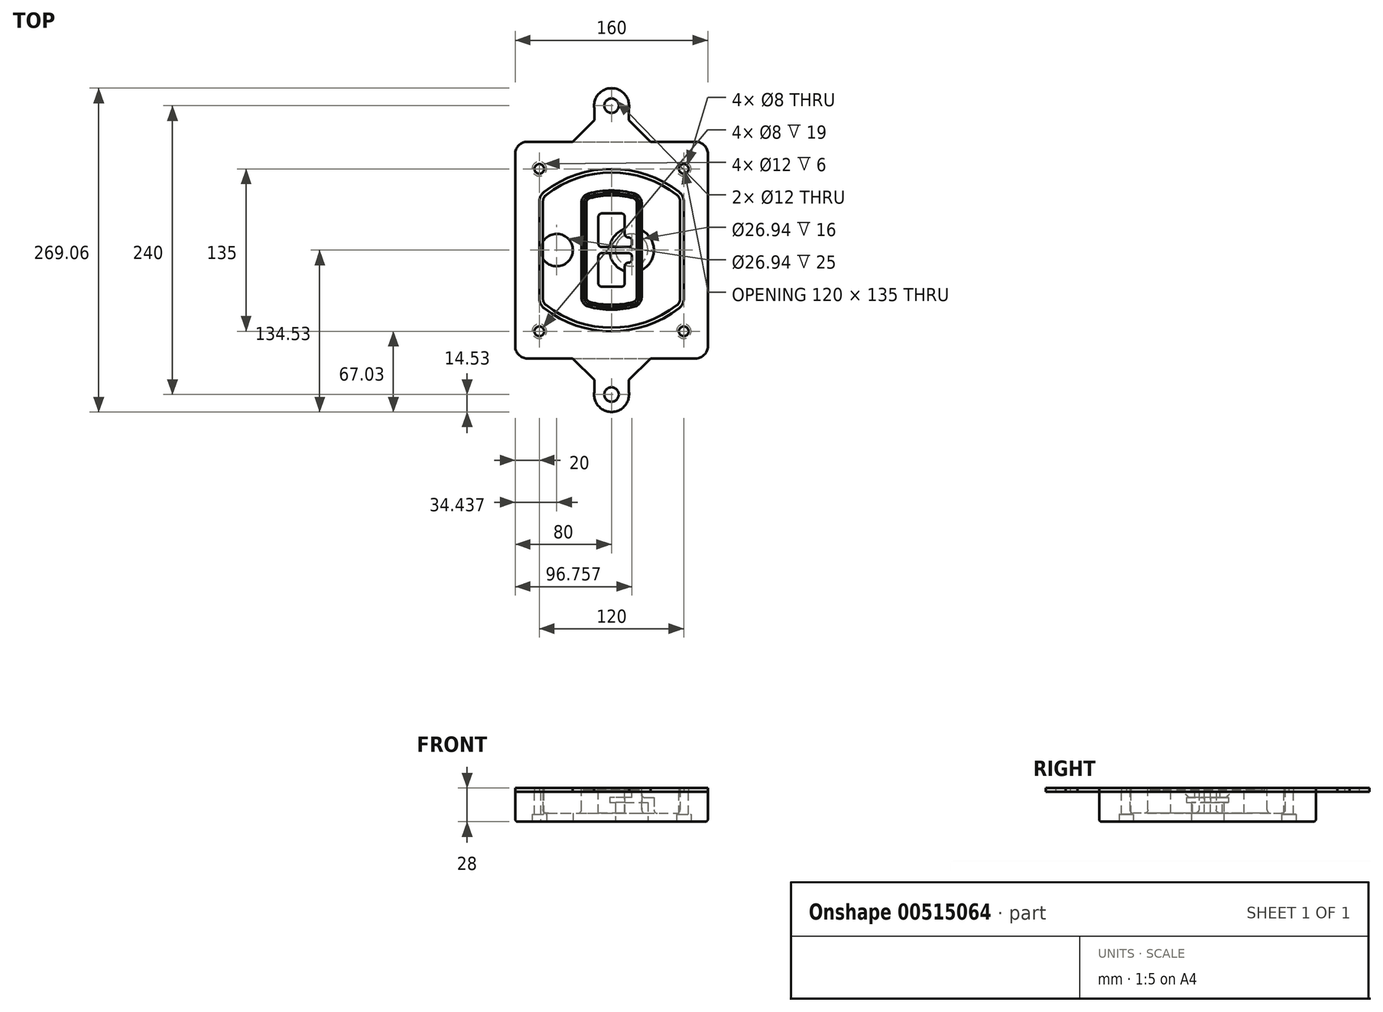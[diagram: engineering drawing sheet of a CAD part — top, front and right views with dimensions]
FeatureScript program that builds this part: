
annotation { "Feature Type Name" : "Feature", "Feature Type Description" : "" }
export const myFeature = defineFeature(function(context is Context, id is Id, definition is map)
    precondition{}
    {
        {
            var Q0;
            Q0=qCreatedBy(makeId("Top.planeOp"),FACE);
            var sketch = newSketch(context, id + "F0", { "sketchPlane" : qUnion([Q0])});
            skPoint(sketch, "E0.rect.middle", {"position": v(0, 0) * mm});
            skLineSegment(sketch, "E1.bottom", {"start": v(-70, -90) * mm, "end": v(70, -90) * mm});
            skLineSegment(sketch, "E1.top", {"start": v(-70, 90) * mm, "end": v(70, 90) * mm});
            skLineSegment(sketch, "E1.left", {"start": v(-80, -80) * mm, "end": v(-80, 80) * mm});
            skLineSegment(sketch, "E1.right", {"start": v(80, -80) * mm, "end": v(80, 80) * mm});
            skLineSegment(sketch, "E2", {"start": v(-80, 90) * mm, "end": v(80, -90) * mm, "construction": true});
            skLineSegment(sketch, "E3", {"start": v(80, 90) * mm, "end": v(-80, -90) * mm, "construction": true});
            skCircle(sketch, "E4", {"center": v(-60, 67.5) * mm, "radius": 4 * mm});
            skCircle(sketch, "E5", {"center": v(60, 67.5) * mm, "radius": 4 * mm});
            skCircle(sketch, "E6", {"center": v(60, -67.5) * mm, "radius": 4 * mm});
            skCircle(sketch, "E7", {"center": v(-60, -67.5) * mm, "radius": 4 * mm});
            skLineSegment(sketch, "E8", {"start": v(-60, 67.5) * mm, "end": v(60, 67.5) * mm, "construction": true});
            skLineSegment(sketch, "E9", {"start": v(60, 67.5) * mm, "end": v(60, -67.5) * mm, "construction": true});
            skLineSegment(sketch, "E10", {"start": v(60, -67.5) * mm, "end": v(-60, -67.5) * mm, "construction": true});
            skLineSegment(sketch, "E11", {"start": v(-60, -67.5) * mm, "end": v(-60, 67.5) * mm, "construction": true});
            skLineSegment(sketch, "E12", {"start": v(-60, 40.3) * mm, "end": v(-60, -40.3) * mm});
            skLineSegment(sketch, "E13", {"start": v(60, 40.3) * mm, "end": v(60, -40.3) * mm});
            skArc(sketch, "E14", {"start": v(56.15, 48.18) * mm, "mid": v(0, 67.5) * mm, "end": v(-56.15, 48.18) * mm});
            skArc(sketch, "E15", {"start": v(-56.15, -48.18) * mm, "mid": v(0, -67.5) * mm, "end": v(56.15, -48.18) * mm});
            skLineSegment(sketch, "E16", {"start": v(-60, 0) * mm, "end": v(60, 0) * mm, "construction": true});
            skPoint(sketch, "E17.visualSharp", {"position": v(-60, -45) * mm});
            skArc(sketch, "E17.filletArc", {"start": v(-60, -40.3) * mm, "mid": v(-58.99, -44.68) * mm, "end": v(-56.15, -48.18) * mm});
            skPoint(sketch, "E18.visualSharp", {"position": v(-60, 45) * mm});
            skArc(sketch, "E18.filletArc", {"start": v(-56.15, 48.18) * mm, "mid": v(-58.99, 44.68) * mm, "end": v(-60, 40.3) * mm});
            skPoint(sketch, "E19.visualSharp", {"position": v(60, 45) * mm});
            skArc(sketch, "E19.filletArc", {"start": v(60, 40.3) * mm, "mid": v(58.99, 44.68) * mm, "end": v(56.15, 48.18) * mm});
            skPoint(sketch, "E20.visualSharp", {"position": v(60, -45) * mm});
            skArc(sketch, "E20.filletArc", {"start": v(56.15, -48.18) * mm, "mid": v(58.99, -44.68) * mm, "end": v(60, -40.3) * mm});
            skPoint(sketch, "E21.visualSharp", {"position": v(-80, 90) * mm});
            skArc(sketch, "E21.filletArc", {"start": v(-70, 90) * mm, "mid": v(-77.07, 87.07) * mm, "end": v(-80, 80) * mm});
            skPoint(sketch, "E22.visualSharp", {"position": v(80, 90) * mm});
            skArc(sketch, "E22.filletArc", {"start": v(80, 80) * mm, "mid": v(77.07, 87.07) * mm, "end": v(70, 90) * mm});
            skPoint(sketch, "E23.visualSharp", {"position": v(80, -90) * mm});
            skArc(sketch, "E23.filletArc", {"start": v(70, -90) * mm, "mid": v(77.07, -87.07) * mm, "end": v(80, -80) * mm});
            skPoint(sketch, "E24.visualSharp", {"position": v(-80, -90) * mm});
            skArc(sketch, "E24.filletArc", {"start": v(-80, -80) * mm, "mid": v(-77.07, -87.07) * mm, "end": v(-70, -90) * mm});
            skArc(sketch, "E25.0", {"start": v(57, 40.3) * mm, "mid": v(56.3, 43.36) * mm, "end": v(54.3, 45.81) * mm});
            skLineSegment(sketch, "E25.1", {"start": v(57, 40.3) * mm, "end": v(57, -40.3) * mm});
            skArc(sketch, "E25.2", {"start": v(54.3, -45.81) * mm, "mid": v(56.3, -43.36) * mm, "end": v(57, -40.3) * mm});
            skArc(sketch, "E25.3", {"start": v(-54.3, -45.81) * mm, "mid": v(0, -64.5) * mm, "end": v(54.3, -45.81) * mm});
            skArc(sketch, "E25.4", {"start": v(-57, -40.3) * mm, "mid": v(-56.3, -43.36) * mm, "end": v(-54.3, -45.81) * mm});
            skArc(sketch, "E25.5", {"start": v(54.3, 45.81) * mm, "mid": v(0, 64.5) * mm, "end": v(-54.3, 45.81) * mm});
            skLineSegment(sketch, "E25.6", {"start": v(-57, 40.3) * mm, "end": v(-57, -40.3) * mm});
            skArc(sketch, "E25.7", {"start": v(-54.3, 45.81) * mm, "mid": v(-56.3, 43.36) * mm, "end": v(-57, 40.3) * mm});
            skArc(sketch, "E26.0", {"start": v(-58.62, 51.33) * mm, "mid": v(-62.58, 46.43) * mm, "end": v(-64, 40.3) * mm});
            skArc(sketch, "E26.1", {"start": v(58.62, 51.33) * mm, "mid": v(0, 71.5) * mm, "end": v(-58.62, 51.33) * mm});
            skArc(sketch, "E26.2", {"start": v(64, 40.3) * mm, "mid": v(62.58, 46.43) * mm, "end": v(58.62, 51.33) * mm});
            skLineSegment(sketch, "E26.3", {"start": v(64, 40.3) * mm, "end": v(64, -40.3) * mm});
            skArc(sketch, "E26.4", {"start": v(58.62, -51.33) * mm, "mid": v(62.58, -46.43) * mm, "end": v(64, -40.3) * mm});
            skLineSegment(sketch, "E26.5", {"start": v(-64, 40.3) * mm, "end": v(-64, -40.3) * mm});
            skArc(sketch, "E26.6", {"start": v(-58.62, -51.33) * mm, "mid": v(0, -71.5) * mm, "end": v(58.62, -51.33) * mm});
            skArc(sketch, "E26.7", {"start": v(-64, -40.3) * mm, "mid": v(-62.58, -46.43) * mm, "end": v(-58.62, -51.33) * mm});
            skSolve(sketch);
        }
        {
            var Q0;
            Q0=makeQuery(id+"F0.imprint","IMPRINT",FACE,{"disambiguationData":[TD([[makeQuery(id+"F0.imprint","IMPRINT",EDGE,{"derivedFrom":sQuery(id+"F0.wireOp",EDGE,"E1.bottom")}),1.0]])]});
            var Q1;
            Q1=makeQuery(id+"F0.imprint","IMPRINT",FACE,{"disambiguationData":[TD([[makeQuery(id+"F0.imprint","IMPRINT",EDGE,{"derivedFrom":sQuery(id+"F0.wireOp",EDGE,"E12")}),1.0]])]});
            var Q2;
            Q2=makeQuery(id+"F0.imprint","IMPRINT",FACE,{"disambiguationData":[TD([[makeQuery(id+"F0.imprint","IMPRINT",EDGE,{"derivedFrom":sQuery(id+"F0.wireOp",EDGE,"E25.0")}),1.0]])]});
            var Q3;
            Q3=makeQuery(id+"F0.imprint","IMPRINT",FACE,{"disambiguationData":[TD([[makeQuery(id+"F0.imprint","IMPRINT",EDGE,{"derivedFrom":sQuery(id+"F0.wireOp",EDGE,"E12")}),-1.0]])]});
            extrude(context, id + "F1", {"entities" : qUnion([Q0, Q1, Q2, Q3]), "oppositeDirection" : true, "depth" : 25 * mm});
        }
        {
            var Q0;
            Q0=makeQuery(id+"F0.imprint","IMPRINT",FACE,{"disambiguationData":[TD([[makeQuery(id+"F0.imprint","IMPRINT",EDGE,{"derivedFrom":sQuery(id+"F0.wireOp",EDGE,"E12")}),1.0]])]});
            extrude(context, id + "F2", {"entities" : qUnion([Q0]), "operationType" : NewBodyOperationType.ADD, "depth" : 3 * mm});
        }
        {
            var Q0;
            Q0=makeQuery(id+"F0.imprint","IMPRINT",FACE,{"disambiguationData":[TD([[makeQuery(id+"F0.imprint","IMPRINT",EDGE,{"derivedFrom":sQuery(id+"F0.wireOp",EDGE,"E25.0")}),1.0]])]});
            extrude(context, id + "F3", {"entities" : qUnion([Q0]), "operationType" : NewBodyOperationType.REMOVE, "oppositeDirection" : true, "depth" : 18 * mm});
        }
        {
            var Q0;
            Q0=makeQuery(id+"F2.opExtrude","CAP_FACE",FACE,{"disambiguationData":[OSD([sQuery(id+"F0.wireOp",EDGE,"E12"),sQuery(id+"F0.wireOp",EDGE,"E13"),sQuery(id+"F0.wireOp",EDGE,"E14"),sQuery(id+"F0.wireOp",EDGE,"E15"),sQuery(id+"F0.wireOp",EDGE,"E17.filletArc"),sQuery(id+"F0.wireOp",EDGE,"E18.filletArc"),sQuery(id+"F0.wireOp",EDGE,"E19.filletArc"),sQuery(id+"F0.wireOp",EDGE,"E20.filletArc"),sQuery(id+"F0.wireOp",EDGE,"E25.0"),sQuery(id+"F0.wireOp",EDGE,"E25.1"),sQuery(id+"F0.wireOp",EDGE,"E25.2"),sQuery(id+"F0.wireOp",EDGE,"E25.3"),sQuery(id+"F0.wireOp",EDGE,"E25.4"),sQuery(id+"F0.wireOp",EDGE,"E25.5"),sQuery(id+"F0.wireOp",EDGE,"E25.6"),sQuery(id+"F0.wireOp",EDGE,"E25.7")])],"isStart":false});
            var sketch = newSketch(context, id + "F4", { "sketchPlane" : qUnion([Q0])});
            skArc(sketch, "E27.0", {"start": v(-19.08, -46.97) * mm, "mid": v(0, -49.5) * mm, "end": v(19.08, -46.97) * mm});
            skArc(sketch, "E28.0", {"start": v(19.08, 46.97) * mm, "mid": v(0, 49.5) * mm, "end": v(-19.08, 46.97) * mm});
            skLineSegment(sketch, "E29", {"start": v(-25, 39.25) * mm, "end": v(-25, -39.25) * mm});
            skLineSegment(sketch, "E30", {"start": v(25, 39.25) * mm, "end": v(25, -39.25) * mm});
            skLineSegment(sketch, "E31", {"start": v(-25, 45.1) * mm, "end": v(25, 45.1) * mm, "construction": true});
            skLineSegment(sketch, "E32", {"start": v(-25, -45.1) * mm, "end": v(25, -45.1) * mm, "construction": true});
            skPoint(sketch, "E33.visualSharp", {"position": v(-25, 45.1) * mm});
            skArc(sketch, "E33.filletArc", {"start": v(-19.08, 46.97) * mm, "mid": v(-23.35, 44.11) * mm, "end": v(-25, 39.25) * mm});
            skPoint(sketch, "E34.visualSharp", {"position": v(25, 45.1) * mm});
            skArc(sketch, "E34.filletArc", {"start": v(25, 39.25) * mm, "mid": v(23.35, 44.11) * mm, "end": v(19.08, 46.97) * mm});
            skPoint(sketch, "E35.visualSharp", {"position": v(25, -45.1) * mm});
            skArc(sketch, "E35.filletArc", {"start": v(19.08, -46.97) * mm, "mid": v(23.35, -44.11) * mm, "end": v(25, -39.25) * mm});
            skPoint(sketch, "E36.visualSharp", {"position": v(-25, -45.1) * mm});
            skArc(sketch, "E36.filletArc", {"start": v(-25, -39.25) * mm, "mid": v(-23.35, -44.11) * mm, "end": v(-19.08, -46.97) * mm});
            skArc(sketch, "E37.0", {"start": v(54.3, 45.81) * mm, "mid": v(0, 64.5) * mm, "end": v(-54.3, 45.81) * mm});
            skArc(sketch, "E37.1", {"start": v(-54.3, 45.81) * mm, "mid": v(-56.3, 43.36) * mm, "end": v(-57, 40.3) * mm});
            skLineSegment(sketch, "E37.2", {"start": v(-57, 40.3) * mm, "end": v(-57, -40.3) * mm});
            skArc(sketch, "E37.3", {"start": v(-57, -40.3) * mm, "mid": v(-56.3, -43.36) * mm, "end": v(-54.3, -45.81) * mm});
            skArc(sketch, "E37.4", {"start": v(-54.3, -45.81) * mm, "mid": v(0, -64.5) * mm, "end": v(54.3, -45.81) * mm});
            skArc(sketch, "E37.5", {"start": v(54.3, -45.81) * mm, "mid": v(56.3, -43.36) * mm, "end": v(57, -40.3) * mm});
            skLineSegment(sketch, "E37.6", {"start": v(57, 40.3) * mm, "end": v(57, -40.3) * mm});
            skArc(sketch, "E37.7", {"start": v(57, 40.3) * mm, "mid": v(56.3, 43.36) * mm, "end": v(54.3, 45.81) * mm});
            skLineSegment(sketch, "E38.0", {"start": v(23, 39.25) * mm, "end": v(23, -39.25) * mm});
            skArc(sketch, "E38.1", {"start": v(18.56, -45.04) * mm, "mid": v(21.76, -42.9) * mm, "end": v(23, -39.25) * mm});
            skArc(sketch, "E38.2", {"start": v(-18.56, -45.04) * mm, "mid": v(0, -47.5) * mm, "end": v(18.56, -45.04) * mm});
            skArc(sketch, "E38.3", {"start": v(-23, -39.25) * mm, "mid": v(-21.76, -42.9) * mm, "end": v(-18.56, -45.04) * mm});
            skLineSegment(sketch, "E38.4", {"start": v(-23, 39.25) * mm, "end": v(-23, -39.25) * mm});
            skArc(sketch, "E38.5", {"start": v(23, 39.25) * mm, "mid": v(21.76, 42.9) * mm, "end": v(18.56, 45.04) * mm});
            skArc(sketch, "E38.6", {"start": v(-18.56, 45.04) * mm, "mid": v(-21.76, 42.9) * mm, "end": v(-23, 39.25) * mm});
            skArc(sketch, "E38.7", {"start": v(18.56, 45.04) * mm, "mid": v(0, 47.5) * mm, "end": v(-18.56, 45.04) * mm});
            skArc(sketch, "E39.0", {"start": v(21, 39.25) * mm, "mid": v(20.18, 41.68) * mm, "end": v(18.04, 43.1) * mm});
            skLineSegment(sketch, "E39.1", {"start": v(21, 39.25) * mm, "end": v(21, -39.25) * mm});
            skArc(sketch, "E39.2", {"start": v(18.04, -43.1) * mm, "mid": v(20.18, -41.68) * mm, "end": v(21, -39.25) * mm});
            skArc(sketch, "E39.3", {"start": v(-18.04, -43.1) * mm, "mid": v(0, -45.5) * mm, "end": v(18.04, -43.1) * mm});
            skArc(sketch, "E39.4", {"start": v(-21, -39.25) * mm, "mid": v(-20.18, -41.68) * mm, "end": v(-18.04, -43.1) * mm});
            skArc(sketch, "E39.5", {"start": v(18.04, 43.1) * mm, "mid": v(0, 45.5) * mm, "end": v(-18.04, 43.1) * mm});
            skLineSegment(sketch, "E39.6", {"start": v(-21, 39.25) * mm, "end": v(-21, -39.25) * mm});
            skArc(sketch, "E39.7", {"start": v(-18.04, 43.1) * mm, "mid": v(-20.18, 41.68) * mm, "end": v(-21, 39.25) * mm});
            skLineSegment(sketch, "E40", {"start": v(-25, 0) * mm, "end": v(25, 0) * mm, "construction": true});
            skLineSegment(sketch, "E41", {"start": v(-11, 5.5) * mm, "end": v(-11, 27.5) * mm});
            skLineSegment(sketch, "E42", {"start": v(-8, 30.5) * mm, "end": v(8, 30.5) * mm});
            skLineSegment(sketch, "E43", {"start": v(11, 27.5) * mm, "end": v(11, 13.5) * mm});
            skLineSegment(sketch, "E44", {"start": v(14, 10.5) * mm, "end": v(14, 10.5) * mm});
            skLineSegment(sketch, "E45", {"start": v(17, 7.5) * mm, "end": v(17, 5.5) * mm});
            skLineSegment(sketch, "E46", {"start": v(14, 2.5) * mm, "end": v(-8, 2.5) * mm});
            skPoint(sketch, "E47.visualSharp", {"position": v(-11, 30.5) * mm});
            skArc(sketch, "E47.filletArc", {"start": v(-8, 30.5) * mm, "mid": v(-10.12, 29.62) * mm, "end": v(-11, 27.5) * mm});
            skPoint(sketch, "E48.visualSharp", {"position": v(11, 30.5) * mm});
            skArc(sketch, "E48.filletArc", {"start": v(11, 27.5) * mm, "mid": v(10.12, 29.62) * mm, "end": v(8, 30.5) * mm});
            skPoint(sketch, "E49.visualSharp", {"position": v(11, 10.5) * mm});
            skArc(sketch, "E49.filletArc", {"start": v(11, 13.5) * mm, "mid": v(11.88, 11.38) * mm, "end": v(14, 10.5) * mm});
            skPoint(sketch, "E50.visualSharp", {"position": v(17, 10.5) * mm});
            skArc(sketch, "E50.filletArc", {"start": v(17, 7.5) * mm, "mid": v(16.12, 9.62) * mm, "end": v(14, 10.5) * mm});
            skPoint(sketch, "E51.visualSharp", {"position": v(17, 2.5) * mm});
            skArc(sketch, "E51.filletArc", {"start": v(14, 2.5) * mm, "mid": v(16.12, 3.38) * mm, "end": v(17, 5.5) * mm});
            skPoint(sketch, "E52.visualSharp", {"position": v(-11, 2.5) * mm});
            skArc(sketch, "E52.filletArc", {"start": v(-11, 5.5) * mm, "mid": v(-10.12, 3.38) * mm, "end": v(-8, 2.5) * mm});
            skLineSegment(sketch, "E53.0.MirrorCS", {"start": v(14, -2.5) * mm, "end": v(-8, -2.5) * mm});
            skArc(sketch, "E54.0.MirrorCS", {"start": v(-11, -5.5) * mm, "mid": v(-10.12, -3.38) * mm, "end": v(-8, -2.5) * mm});
            skLineSegment(sketch, "E55.0.MirrorCS", {"start": v(-11, -5.5) * mm, "end": v(-11, -27.5) * mm});
            skArc(sketch, "E56.0.MirrorCS", {"start": v(-8, -30.5) * mm, "mid": v(-10.12, -29.62) * mm, "end": v(-11, -27.5) * mm});
            skLineSegment(sketch, "E57.0.MirrorCS", {"start": v(-8, -30.5) * mm, "end": v(8, -30.5) * mm});
            skArc(sketch, "E58.0.MirrorCS", {"start": v(11, -27.5) * mm, "mid": v(10.12, -29.62) * mm, "end": v(8, -30.5) * mm});
            skLineSegment(sketch, "E59.0.MirrorCS", {"start": v(11, -27.5) * mm, "end": v(11, -13.5) * mm});
            skArc(sketch, "E60.0.MirrorCS", {"start": v(11, -13.5) * mm, "mid": v(11.88, -11.38) * mm, "end": v(14, -10.5) * mm});
            skArc(sketch, "E61.0.MirrorCS", {"start": v(17, -7.5) * mm, "mid": v(16.12, -9.62) * mm, "end": v(14, -10.5) * mm});
            skLineSegment(sketch, "E62.0.MirrorCS", {"start": v(17, -7.5) * mm, "end": v(17, -5.5) * mm});
            skArc(sketch, "E63.0.MirrorCS", {"start": v(14, -2.5) * mm, "mid": v(16.12, -3.38) * mm, "end": v(17, -5.5) * mm});
            skSolve(sketch);
        }
        {
            var Q0;
            Q0=makeQuery(id+"F4.imprint","IMPRINT",FACE,{"disambiguationData":[TD([[makeQuery(id+"F4.imprint","IMPRINT",EDGE,{"derivedFrom":sQuery(id+"F4.wireOp",EDGE,"E27.0")}),1.0]])]});
            var Q1;
            Q1=makeQuery(id+"F4.imprint","IMPRINT",FACE,{"disambiguationData":[TD([[makeQuery(id+"F4.imprint","IMPRINT",EDGE,{"derivedFrom":sQuery(id+"F4.wireOp",EDGE,"E38.0")}),-1.0]])]});
            var Q2;
            Q2=makeQuery(id+"F4.imprint","IMPRINT",FACE,{"disambiguationData":[TD([[makeQuery(id+"F4.imprint","IMPRINT",EDGE,{"derivedFrom":sQuery(id+"F4.wireOp",EDGE,"E39.0")}),1.0]])]});
            extrude(context, id + "F5", {"entities" : qUnion([Q0, Q1, Q2]), "operationType" : NewBodyOperationType.ADD, "endBound" : BoundingType.UP_TO_NEXT, "oppositeDirection" : true, "depth" : 25 * mm});
        }
        {
            var Q0;
            Q0=makeQuery(id+"F4.imprint","IMPRINT",FACE,{"disambiguationData":[TD([[makeQuery(id+"F4.imprint","IMPRINT",EDGE,{"derivedFrom":sQuery(id+"F4.wireOp",EDGE,"E38.0")}),-1.0]])]});
            extrude(context, id + "F6", {"entities" : qUnion([Q0]), "operationType" : NewBodyOperationType.REMOVE, "oppositeDirection" : true, "depth" : 2 * mm});
        }
        {
            var Q0;
            Q0=makeQuery(id+"F1.opExtrude","CAP_FACE",FACE,{"disambiguationData":[OSD([sQuery(id+"F0.wireOp",EDGE,"E1.bottom"),sQuery(id+"F0.wireOp",EDGE,"E1.top"),sQuery(id+"F0.wireOp",EDGE,"E1.left"),sQuery(id+"F0.wireOp",EDGE,"E1.right"),sQuery(id+"F0.wireOp",EDGE,"E4"),sQuery(id+"F0.wireOp",EDGE,"E5"),sQuery(id+"F0.wireOp",EDGE,"E6"),sQuery(id+"F0.wireOp",EDGE,"E7"),sQuery(id+"F0.wireOp",EDGE,"E21.filletArc"),sQuery(id+"F0.wireOp",EDGE,"E22.filletArc"),sQuery(id+"F0.wireOp",EDGE,"E23.filletArc"),sQuery(id+"F0.wireOp",EDGE,"E24.filletArc")])],"isStart":false});
            var sketch = newSketch(context, id + "F7", { "sketchPlane" : qUnion([Q0])});
            skCircle(sketch, "E64", {"center": v(16.76, 0) * mm, "radius": 13.47 * mm});
            skCircle(sketch, "E65", {"center": v(-45.56, 0) * mm, "radius": 13.47 * mm});
            skLineSegment(sketch, "E66", {"start": v(80, 0) * mm, "end": v(-80, 0) * mm});
            skCircle(sketch, "E67", {"center": v(16.76, 0) * mm, "radius": 18.47 * mm});
            skCircle(sketch, "E68", {"center": v(60, -67.5) * mm, "radius": 6 * mm});
            skCircle(sketch, "E69", {"center": v(-60, -67.5) * mm, "radius": 6 * mm});
            skCircle(sketch, "E70", {"center": v(-60, 67.5) * mm, "radius": 6 * mm});
            skCircle(sketch, "E71", {"center": v(60, 67.5) * mm, "radius": 6 * mm});
            skSolve(sketch);
        }
        {
            var Q0;
            {var subQ1=sQuery(id+"F7.wireOp",EDGE,"E66");var subQ4=sQuery(id+"F7.wireOp",EDGE,"E64");var subQ6=makeQuery(id+"F7.imprint","INTERSECT",VERTEX,{"disambiguationData":[OD(0.0)],"derivedFrom":[subQ4,subQ1]});Q0=makeQuery(id+"F7.imprint","IMPRINT",FACE,{"disambiguationData":[TD([[makeQuery(id+"F7.imprint","IMPRINT",EDGE,{"disambiguationData":[TD([[subQ6,-1.0]])],"derivedFrom":subQ4}),-1.0]])]});}
            var Q1;
            {var subQ0=sQuery(id+"F7.wireOp",EDGE,"E66");var subQ1=sQuery(id+"F7.wireOp",EDGE,"E64");var subQ3=makeQuery(id+"F7.imprint","INTERSECT",VERTEX,{"disambiguationData":[OD(0.0)],"derivedFrom":[subQ1,subQ0]});Q1=makeQuery(id+"F7.imprint","IMPRINT",FACE,{"disambiguationData":[TD([[makeQuery(id+"F7.imprint","IMPRINT",EDGE,{"disambiguationData":[TD([[subQ3,-1.0]])],"derivedFrom":subQ1}),1.0]])]});}
            var Q2;
            {var subQ0=sQuery(id+"F7.wireOp",EDGE,"E66");var subQ1=sQuery(id+"F7.wireOp",EDGE,"E64");var subQ3=makeQuery(id+"F7.imprint","INTERSECT",VERTEX,{"disambiguationData":[OD(0.0)],"derivedFrom":[subQ1,subQ0]});Q2=makeQuery(id+"F7.imprint","IMPRINT",FACE,{"disambiguationData":[TD([[makeQuery(id+"F7.imprint","IMPRINT",EDGE,{"disambiguationData":[TD([[subQ3,1.0]])],"derivedFrom":subQ1}),1.0]])]});}
            var Q3;
            {var subQ1=sQuery(id+"F7.wireOp",EDGE,"E66");var subQ4=sQuery(id+"F7.wireOp",EDGE,"E64");var subQ6=makeQuery(id+"F7.imprint","INTERSECT",VERTEX,{"disambiguationData":[OD(0.0)],"derivedFrom":[subQ4,subQ1]});Q3=makeQuery(id+"F7.imprint","IMPRINT",FACE,{"disambiguationData":[TD([[makeQuery(id+"F7.imprint","IMPRINT",EDGE,{"disambiguationData":[TD([[subQ6,1.0]])],"derivedFrom":subQ4}),-1.0]])]});}
            extrude(context, id + "F8", {"entities" : qUnion([Q0, Q1, Q2, Q3]), "operationType" : NewBodyOperationType.ADD, "oppositeDirection" : true, "depth" : 20 * mm});
        }
        {
            var Q0;
            {var subQ0=sQuery(id+"F7.wireOp",EDGE,"E66");var subQ1=sQuery(id+"F7.wireOp",EDGE,"E64");var subQ3=makeQuery(id+"F7.imprint","INTERSECT",VERTEX,{"disambiguationData":[OD(0.0)],"derivedFrom":[subQ1,subQ0]});Q0=makeQuery(id+"F7.imprint","IMPRINT",FACE,{"disambiguationData":[TD([[makeQuery(id+"F7.imprint","IMPRINT",EDGE,{"disambiguationData":[TD([[subQ3,-1.0]])],"derivedFrom":subQ1}),1.0]])]});}
            var Q1;
            {var subQ0=sQuery(id+"F7.wireOp",EDGE,"E66");var subQ1=sQuery(id+"F7.wireOp",EDGE,"E64");var subQ3=makeQuery(id+"F7.imprint","INTERSECT",VERTEX,{"disambiguationData":[OD(0.0)],"derivedFrom":[subQ1,subQ0]});Q1=makeQuery(id+"F7.imprint","IMPRINT",FACE,{"disambiguationData":[TD([[makeQuery(id+"F7.imprint","IMPRINT",EDGE,{"disambiguationData":[TD([[subQ3,1.0]])],"derivedFrom":subQ1}),1.0]])]});}
            extrude(context, id + "F9", {"entities" : qUnion([Q0, Q1]), "operationType" : NewBodyOperationType.REMOVE, "oppositeDirection" : true, "depth" : 16 * mm});
        }
        {
            var Q0;
            {var subQ0=sQuery(id+"F7.wireOp",EDGE,"E66");var subQ1=sQuery(id+"F7.wireOp",EDGE,"E65");var subQ3=makeQuery(id+"F7.imprint","INTERSECT",VERTEX,{"disambiguationData":[OD(0.0)],"derivedFrom":[subQ1,subQ0]});Q0=makeQuery(id+"F7.imprint","IMPRINT",FACE,{"disambiguationData":[TD([[makeQuery(id+"F7.imprint","IMPRINT",EDGE,{"disambiguationData":[TD([[subQ3,-1.0]])],"derivedFrom":subQ1}),1.0]])]});}
            var Q1;
            {var subQ0=sQuery(id+"F7.wireOp",EDGE,"E66");var subQ1=sQuery(id+"F7.wireOp",EDGE,"E65");var subQ3=makeQuery(id+"F7.imprint","INTERSECT",VERTEX,{"disambiguationData":[OD(0.0)],"derivedFrom":[subQ1,subQ0]});Q1=makeQuery(id+"F7.imprint","IMPRINT",FACE,{"disambiguationData":[TD([[makeQuery(id+"F7.imprint","IMPRINT",EDGE,{"disambiguationData":[TD([[subQ3,1.0]])],"derivedFrom":subQ1}),1.0]])]});}
            extrude(context, id + "F10", {"entities" : qUnion([Q0, Q1]), "operationType" : NewBodyOperationType.REMOVE, "oppositeDirection" : true, "depth" : 25 * mm});
        }
        {
            var Q0;
            Q0=makeQuery(id+"F7.imprint","IMPRINT",FACE,{"disambiguationData":[TD([[makeQuery(id+"F7.imprint","IMPRINT",EDGE,{"derivedFrom":sQuery(id+"F7.wireOp",EDGE,"E68")}),1.0]])]});
            var Q1;
            Q1=makeQuery(id+"F7.imprint","IMPRINT",FACE,{"disambiguationData":[TD([[makeQuery(id+"F7.imprint","IMPRINT",EDGE,{"derivedFrom":makeQuery(id+"F1.opExtrude","CAP_EDGE",EDGE,{"disambiguationData":[OSD([sQuery(id+"F0.wireOp",EDGE,"E5")])],"isStart":false})}),-1.0]])]});
            var Q2;
            Q2=makeQuery(id+"F7.imprint","IMPRINT",FACE,{"disambiguationData":[TD([[makeQuery(id+"F7.imprint","IMPRINT",EDGE,{"derivedFrom":sQuery(id+"F7.wireOp",EDGE,"E69")}),1.0]])]});
            var Q3;
            Q3=makeQuery(id+"F7.imprint","IMPRINT",FACE,{"disambiguationData":[TD([[makeQuery(id+"F7.imprint","IMPRINT",EDGE,{"derivedFrom":makeQuery(id+"F1.opExtrude","CAP_EDGE",EDGE,{"disambiguationData":[OSD([sQuery(id+"F0.wireOp",EDGE,"E4")])],"isStart":false})}),-1.0]])]});
            var Q4;
            Q4=makeQuery(id+"F7.imprint","IMPRINT",FACE,{"disambiguationData":[TD([[makeQuery(id+"F7.imprint","IMPRINT",EDGE,{"derivedFrom":sQuery(id+"F7.wireOp",EDGE,"E70")}),1.0]])]});
            var Q5;
            Q5=makeQuery(id+"F7.imprint","IMPRINT",FACE,{"disambiguationData":[TD([[makeQuery(id+"F7.imprint","IMPRINT",EDGE,{"derivedFrom":makeQuery(id+"F1.opExtrude","CAP_EDGE",EDGE,{"disambiguationData":[OSD([sQuery(id+"F0.wireOp",EDGE,"E7")])],"isStart":false})}),-1.0]])]});
            var Q6;
            Q6=makeQuery(id+"F7.imprint","IMPRINT",FACE,{"disambiguationData":[TD([[makeQuery(id+"F7.imprint","IMPRINT",EDGE,{"derivedFrom":sQuery(id+"F7.wireOp",EDGE,"E71")}),1.0]])]});
            var Q7;
            Q7=makeQuery(id+"F7.imprint","IMPRINT",FACE,{"disambiguationData":[TD([[makeQuery(id+"F7.imprint","IMPRINT",EDGE,{"derivedFrom":makeQuery(id+"F1.opExtrude","CAP_EDGE",EDGE,{"disambiguationData":[OSD([sQuery(id+"F0.wireOp",EDGE,"E6")])],"isStart":false})}),-1.0]])]});
            extrude(context, id + "F11", {"entities" : qUnion([Q0, Q1, Q2, Q3, Q4, Q5, Q6, Q7]), "operationType" : NewBodyOperationType.REMOVE, "oppositeDirection" : true, "depth" : 6 * mm});
        }
        {
            var Q0;
            Q0=makeQuery(id+"F9.boolean.opBoolean","COPY",FACE,{"derivedFrom":makeQuery(id+"F9.opExtrude","CAP_FACE",FACE,{"disambiguationData":[OSD([sQuery(id+"F7.wireOp",EDGE,"E64")])],"isStart":false})});
            var sketch = newSketch(context, id + "F12", { "sketchPlane" : qUnion([Q0])});
            skArc(sketch, "E72.0", {"start": v(11, 17.55) * mm, "mid": v(2.57, 11.82) * mm, "end": v(-1.54, 2.5) * mm});
            skArc(sketch, "E72.1", {"start": v(-1.54, -2.5) * mm, "mid": v(2.57, -11.82) * mm, "end": v(11, -17.55) * mm});
            skLineSegment(sketch, "E73", {"start": v(-1.54, -2.5) * mm, "end": v(14, -2.5) * mm});
            skLineSegment(sketch, "E74.0", {"start": v(14, 2.5) * mm, "end": v(-1.54, 2.5) * mm});
            skArc(sketch, "E74.1", {"start": v(14, 2.5) * mm, "mid": v(16.12, 3.38) * mm, "end": v(17, 5.5) * mm});
            skLineSegment(sketch, "E74.2", {"start": v(17, 7.5) * mm, "end": v(17, 5.5) * mm});
            skArc(sketch, "E74.3", {"start": v(17, 7.5) * mm, "mid": v(16.12, 9.62) * mm, "end": v(14, 10.5) * mm});
            skArc(sketch, "E74.4", {"start": v(11, 13.5) * mm, "mid": v(11.88, 11.38) * mm, "end": v(14, 10.5) * mm});
            skLineSegment(sketch, "E74.5", {"start": v(11, 17.55) * mm, "end": v(11, 13.5) * mm});
            skLineSegment(sketch, "E74.7", {"start": v(14, -2.5) * mm, "end": v(-1.54, -2.5) * mm});
            skArc(sketch, "E74.8", {"start": v(14, -2.5) * mm, "mid": v(16.12, -3.38) * mm, "end": v(17, -5.5) * mm});
            skLineSegment(sketch, "E74.9", {"start": v(17, -7.5) * mm, "end": v(17, -5.5) * mm});
            skArc(sketch, "E74.10", {"start": v(17, -7.5) * mm, "mid": v(16.12, -9.62) * mm, "end": v(14, -10.5) * mm});
            skArc(sketch, "E74.11", {"start": v(11, -13.5) * mm, "mid": v(11.88, -11.38) * mm, "end": v(14, -10.5) * mm});
            skLineSegment(sketch, "E74.12", {"start": v(11, -17.55) * mm, "end": v(11, -13.5) * mm});
            skPoint(sketch, "E75.orphan", {"position": v(11, -27.5) * mm});
            skPoint(sketch, "E76.orphan", {"position": v(-8, -2.5) * mm});
            skPoint(sketch, "E77.orphan", {"position": v(-8, 2.5) * mm});
            skPoint(sketch, "E78.orphan", {"position": v(11, 27.5) * mm});
            skSolve(sketch);
        }
        {
            var Q0;
            {var subQ7=sQuery(id+"F12.wireOp",EDGE,"E72.0");var subQ14=sQuery(id+"F12.wireOp",EDGE,"E72.1");var subQ16=sQuery(id+"F12.wireOp",EDGE,"E74.1");var subQ18=sQuery(id+"F12.wireOp",EDGE,"E74.8");Q0=qUnion([makeQuery(id+"F12.imprint","IMPRINT",FACE,{"disambiguationData":[TD([[makeQuery(id+"F12.imprint","IMPRINT",EDGE,{"derivedFrom":subQ7}),1.0]])]}),makeQuery(id+"F12.imprint","IMPRINT",FACE,{"disambiguationData":[TD([[makeQuery(id+"F12.imprint","IMPRINT",EDGE,{"derivedFrom":subQ14}),1.0]])]}),makeQuery(id+"F12.imprint","IMPRINT",FACE,{"disambiguationData":[TD([[makeQuery(id+"F12.imprint","IMPRINT",EDGE,{"derivedFrom":subQ16}),1.0]])]}),makeQuery(id+"F12.imprint","IMPRINT",FACE,{"disambiguationData":[TD([[makeQuery(id+"F12.imprint","IMPRINT",EDGE,{"derivedFrom":subQ18}),-1.0]])]})]);}
            var Q1;
            Q1=makeQuery(id+"F5.boolean.opBoolean","SPLIT",FACE,{"disambiguationData":[TD([makeQuery(id+"F5.opExtrude","SWEPT_FACE",FACE,{"disambiguationData":[OSD([sQuery(id+"F4.wireOp",EDGE,"E41")])]})])],"derivedFrom":makeQuery(id+"F3.boolean.opBoolean","COPY",FACE,{"derivedFrom":makeQuery(id+"F3.opExtrude","CAP_FACE",FACE,{"disambiguationData":[OSD([sQuery(id+"F0.wireOp",EDGE,"E25.0"),sQuery(id+"F0.wireOp",EDGE,"E25.1"),sQuery(id+"F0.wireOp",EDGE,"E25.2"),sQuery(id+"F0.wireOp",EDGE,"E25.3"),sQuery(id+"F0.wireOp",EDGE,"E25.4"),sQuery(id+"F0.wireOp",EDGE,"E25.5"),sQuery(id+"F0.wireOp",EDGE,"E25.6"),sQuery(id+"F0.wireOp",EDGE,"E25.7")])],"isStart":false})})});
            extrude(context, id + "F13", {"entities" : qUnion([Q0]), "operationType" : NewBodyOperationType.REMOVE, "endBound" : BoundingType.UP_TO_SURFACE, "endBoundEntityFace" : qUnion([Q1]), "depth" : 25 * mm});
        }
        {
            var Q0;
            Q0=makeQuery(id+"F3.boolean.opBoolean","COPY",EDGE,{"derivedFrom":makeQuery(id+"F3.opExtrude","CAP_EDGE",EDGE,{"disambiguationData":[OSD([sQuery(id+"F0.wireOp",EDGE,"E25.6")])],"isStart":false})});
            var Q1;
            Q1=makeQuery(id+"F8.boolean.opBoolean","INTERSECT",EDGE,{"derivedFrom":[makeQuery(id+"F5.opExtrude","SWEPT_FACE",FACE,{"disambiguationData":[OSD([sQuery(id+"F4.wireOp",EDGE,"E30")])]}),makeQuery(id+"F8.opExtrude","CAP_FACE",FACE,{"disambiguationData":[OSD([sQuery(id+"F7.wireOp",EDGE,"E67")])],"isStart":false})]});
            var Q2;
            Q2=makeQuery(id+"F8.boolean.opBoolean","INTERSECT",EDGE,{"disambiguationData":[OD(1.0)],"derivedFrom":[makeQuery(id+"F5.opExtrude","SWEPT_FACE",FACE,{"disambiguationData":[OSD([sQuery(id+"F4.wireOp",EDGE,"E30")])]}),makeQuery(id+"F8.opExtrude","SWEPT_FACE",FACE,{"disambiguationData":[OSD([sQuery(id+"F7.wireOp",EDGE,"E67")])]})]});
            var Q3;
            {var subQ0=sQuery(id+"F4.wireOp",EDGE,"E30");Q3=makeQuery(id+"F8.boolean.opBoolean","SPLIT",EDGE,{"disambiguationData":[TD([makeQuery(id+"F5.opExtrude","SWEPT_FACE",FACE,{"disambiguationData":[OSD([sQuery(id+"F4.wireOp",EDGE,"E35.filletArc")])]})])],"derivedFrom":makeQuery(id+"F5.opExtrude","CAP_EDGE",EDGE,{"disambiguationData":[OSD([subQ0])],"isStart":false})});}
            var Q4;
            {var subQ0=sQuery(id+"F0.wireOp",EDGE,"E25.7");var subQ1=sQuery(id+"F0.wireOp",EDGE,"E25.1");var subQ2=sQuery(id+"F0.wireOp",EDGE,"E25.6");var subQ3=sQuery(id+"F0.wireOp",EDGE,"E25.5");var subQ4=sQuery(id+"F0.wireOp",EDGE,"E25.4");var subQ5=sQuery(id+"F0.wireOp",EDGE,"E25.0");var subQ6=sQuery(id+"F0.wireOp",EDGE,"E25.2");var subQ7=sQuery(id+"F0.wireOp",EDGE,"E25.3");Q4=makeQuery(id+"F8.boolean.opBoolean","INTERSECT",EDGE,{"derivedFrom":[makeQuery(id+"F5.boolean.opBoolean","SPLIT",FACE,{"disambiguationData":[TD([makeQuery(id+"F2.opExtrude","SWEPT_FACE",FACE,{"disambiguationData":[OSD([subQ5])]})])],"derivedFrom":makeQuery(id+"F3.boolean.opBoolean","COPY",FACE,{"derivedFrom":makeQuery(id+"F3.opExtrude","CAP_FACE",FACE,{"disambiguationData":[OSD([subQ5,subQ1,subQ6,subQ7,subQ4,subQ3,subQ2,subQ0])],"isStart":false})})}),makeQuery(id+"F8.opExtrude","SWEPT_FACE",FACE,{"disambiguationData":[OSD([sQuery(id+"F7.wireOp",EDGE,"E67")])]})]});}
            var Q5;
            Q5=makeQuery(id+"F8.boolean.opBoolean","INTERSECT",EDGE,{"disambiguationData":[OD(0.0)],"derivedFrom":[makeQuery(id+"F5.opExtrude","SWEPT_FACE",FACE,{"disambiguationData":[OSD([sQuery(id+"F4.wireOp",EDGE,"E30")])]}),makeQuery(id+"F8.opExtrude","SWEPT_FACE",FACE,{"disambiguationData":[OSD([sQuery(id+"F7.wireOp",EDGE,"E67")])]})]});
            fillet(context, id + "F14", {"entities" : qUnion([Q0, Q1, Q2, Q3, Q4, Q5]), "radius" : 3 * mm, "tangentPropagation" : true, "allowEdgeOverflow" : false});
        }
        {
            var Q0;
            Q0=makeQuery(id+"F1.opExtrude","CAP_EDGE",EDGE,{"disambiguationData":[OSD([sQuery(id+"F0.wireOp",EDGE,"E1.bottom")])],"isStart":false});
            fillet(context, id + "F15", {"entities" : qUnion([Q0]), "radius" : 2 * mm, "tangentPropagation" : true, "allowEdgeOverflow" : false});
        }
        {
            var Q0;
            {var subQ0=sQuery(id+"F0.wireOp",EDGE,"E21.filletArc");var subQ1=sQuery(id+"F0.wireOp",EDGE,"E7");var subQ2=sQuery(id+"F0.wireOp",EDGE,"E6");var subQ3=sQuery(id+"F0.wireOp",EDGE,"E5");var subQ4=sQuery(id+"F0.wireOp",EDGE,"E4");var subQ5=sQuery(id+"F0.wireOp",EDGE,"E22.filletArc");var subQ6=sQuery(id+"F0.wireOp",EDGE,"E1.bottom");var subQ7=sQuery(id+"F0.wireOp",EDGE,"E1.right");var subQ8=sQuery(id+"F0.wireOp",EDGE,"E1.top");var subQ9=sQuery(id+"F0.wireOp",EDGE,"E1.left");var subQ10=sQuery(id+"F0.wireOp",EDGE,"E23.filletArc");var subQ11=sQuery(id+"F0.wireOp",EDGE,"E24.filletArc");Q0=makeQuery(id+"F2.boolean.opBoolean","SPLIT",FACE,{"disambiguationData":[TD([makeQuery(id+"F1.opExtrude","SWEPT_FACE",FACE,{"disambiguationData":[OSD([subQ6])]})])],"derivedFrom":makeQuery(id+"F1.opExtrude","CAP_FACE",FACE,{"disambiguationData":[OSD([subQ6,subQ8,subQ9,subQ7,subQ4,subQ3,subQ2,subQ1,subQ0,subQ5,subQ10,subQ11])],"isStart":true})});}
            var sketch = newSketch(context, id + "F16", { "sketchPlane" : qUnion([Q0])});
            skLineSegment(sketch, "E79.0", {"start": v(-80, -80) * mm, "end": v(-80, 80) * mm});
            skArc(sketch, "E79.1", {"start": v(-70, 90) * mm, "mid": v(-77.07, 87.07) * mm, "end": v(-80, 80) * mm});
            skLineSegment(sketch, "E80.0", {"start": v(-70, 90) * mm, "end": v(70, 90) * mm});
            skArc(sketch, "E80.1", {"start": v(80, 80) * mm, "mid": v(77.07, 87.07) * mm, "end": v(70, 90) * mm});
            skLineSegment(sketch, "E80.2", {"start": v(80, -80) * mm, "end": v(80, 80) * mm});
            skArc(sketch, "E81.0", {"start": v(-80, -80) * mm, "mid": v(-77.07, -87.07) * mm, "end": v(-70, -90) * mm});
            skArc(sketch, "E81.1", {"start": v(-80, -80) * mm, "mid": v(-77.07, -87.07) * mm, "end": v(-70, -90) * mm});
            skLineSegment(sketch, "E82.0", {"start": v(-70, -90) * mm, "end": v(70, -90) * mm});
            skArc(sketch, "E83.0", {"start": v(-56.15, -48.18) * mm, "mid": v(0, -67.5) * mm, "end": v(56.15, -48.18) * mm});
            skLineSegment(sketch, "E84.0", {"start": v(60, 40.3) * mm, "end": v(60, -40.3) * mm});
            skArc(sketch, "E85.0", {"start": v(56.15, 48.18) * mm, "mid": v(0, 67.5) * mm, "end": v(-56.15, 48.18) * mm});
            skArc(sketch, "E86.0", {"start": v(60, 40.3) * mm, "mid": v(58.99, 44.68) * mm, "end": v(56.15, 48.18) * mm});
            skArc(sketch, "E86.1", {"start": v(56.15, -48.18) * mm, "mid": v(58.99, -44.68) * mm, "end": v(60, -40.3) * mm});
            skArc(sketch, "E87.0", {"start": v(-56.15, 48.18) * mm, "mid": v(-58.99, 44.68) * mm, "end": v(-60, 40.3) * mm});
            skLineSegment(sketch, "E87.1", {"start": v(-60, 40.3) * mm, "end": v(-60, -40.3) * mm});
            skArc(sketch, "E87.2", {"start": v(-60, -40.3) * mm, "mid": v(-58.99, -44.68) * mm, "end": v(-56.15, -48.18) * mm});
            skLineSegment(sketch, "E88", {"start": v(-80, 0) * mm, "end": v(80, 0) * mm, "construction": true});
            skLineSegment(sketch, "E89", {"start": v(0, 90) * mm, "end": v(0, 120) * mm, "construction": true});
            skCircle(sketch, "E90", {"center": v(0, 120) * mm, "radius": 6 * mm});
            skLineSegment(sketch, "E91", {"start": v(-32.33, 90) * mm, "end": v(-14.33, 108) * mm});
            skLineSegment(sketch, "E92", {"start": v(-14.33, 108) * mm, "end": v(-14.33, 118) * mm});
            skLineSegment(sketch, "E93", {"start": v(14.42, 118) * mm, "end": v(14.42, 108) * mm});
            skLineSegment(sketch, "E94", {"start": v(14.42, 108) * mm, "end": v(32.42, 90) * mm});
            skArc(sketch, "E95", {"start": v(14.42, 118) * mm, "mid": v(0.04, 134.53) * mm, "end": v(-14.33, 118) * mm});
            skLineSegment(sketch, "E96.MirrorCS", {"start": v(0, -90) * mm, "end": v(0, -120) * mm, "construction": true});
            skLineSegment(sketch, "E97.MirrorCS", {"start": v(14.42, -108) * mm, "end": v(32.42, -90) * mm});
            skLineSegment(sketch, "E98.MirrorCS", {"start": v(-32.33, -90) * mm, "end": v(-14.33, -108) * mm});
            skLineSegment(sketch, "E99.MirrorCS", {"start": v(-14.33, -108) * mm, "end": v(-14.33, -118) * mm});
            skArc(sketch, "E100.MirrorCS", {"start": v(14.42, -118) * mm, "mid": v(0.04, -134.53) * mm, "end": v(-14.33, -118) * mm});
            skLineSegment(sketch, "E101.MirrorCS", {"start": v(14.42, -118) * mm, "end": v(14.42, -108) * mm});
            skCircle(sketch, "E102.MirrorC", {"center": v(0, -120) * mm, "radius": 6 * mm});
            skArc(sketch, "E103.0", {"start": v(54.3, 45.81) * mm, "mid": v(0, 64.5) * mm, "end": v(-54.3, 45.81) * mm});
            skArc(sketch, "E103.1", {"start": v(-54.3, 45.81) * mm, "mid": v(-56.3, 43.36) * mm, "end": v(-57, 40.3) * mm});
            skLineSegment(sketch, "E103.2", {"start": v(-57, 40.3) * mm, "end": v(-57, -40.3) * mm});
            skArc(sketch, "E103.3", {"start": v(57, 40.3) * mm, "mid": v(56.3, 43.36) * mm, "end": v(54.3, 45.81) * mm});
            skLineSegment(sketch, "E103.4", {"start": v(57, 40.3) * mm, "end": v(57, -40.3) * mm});
            skArc(sketch, "E103.5", {"start": v(54.3, -45.81) * mm, "mid": v(56.3, -43.36) * mm, "end": v(57, -40.3) * mm});
            skArc(sketch, "E103.6", {"start": v(-54.3, -45.81) * mm, "mid": v(0, -64.5) * mm, "end": v(54.3, -45.81) * mm});
            skArc(sketch, "E103.7", {"start": v(-57, -40.3) * mm, "mid": v(-56.3, -43.36) * mm, "end": v(-54.3, -45.81) * mm});
            skSolve(sketch);
        }
        {
            var Q0;
            Q0=makeQuery(id+"F16.imprint","IMPRINT",FACE,{"disambiguationData":[TD([[makeQuery(id+"F16.imprint","IMPRINT",EDGE,{"derivedFrom":sQuery(id+"F16.wireOp",EDGE,"E90")}),-1.0]])]});
            var Q1;
            Q1=makeQuery(id+"F16.imprint","IMPRINT",FACE,{"disambiguationData":[TD([[makeQuery(id+"F16.imprint","IMPRINT",EDGE,{"derivedFrom":sQuery(id+"F16.wireOp",EDGE,"E79.0")}),-1.0]])]});
            var Q2;
            {var subQ1=sQuery(id+"F16.wireOp",EDGE,"E97.MirrorCS");Q2=makeQuery(id+"F16.imprint","IMPRINT",FACE,{"disambiguationData":[TD([[makeQuery(id+"F16.imprint","IMPRINT",EDGE,{"derivedFrom":subQ1}),1.0]])]});}
            var Q3;
            Q3=makeQuery(id+"F2.opExtrude","CAP_FACE",FACE,{"disambiguationData":[OSD([sQuery(id+"F0.wireOp",EDGE,"E12"),sQuery(id+"F0.wireOp",EDGE,"E13"),sQuery(id+"F0.wireOp",EDGE,"E14"),sQuery(id+"F0.wireOp",EDGE,"E15"),sQuery(id+"F0.wireOp",EDGE,"E17.filletArc"),sQuery(id+"F0.wireOp",EDGE,"E18.filletArc"),sQuery(id+"F0.wireOp",EDGE,"E19.filletArc"),sQuery(id+"F0.wireOp",EDGE,"E20.filletArc"),sQuery(id+"F0.wireOp",EDGE,"E25.0"),sQuery(id+"F0.wireOp",EDGE,"E25.1"),sQuery(id+"F0.wireOp",EDGE,"E25.2"),sQuery(id+"F0.wireOp",EDGE,"E25.3"),sQuery(id+"F0.wireOp",EDGE,"E25.4"),sQuery(id+"F0.wireOp",EDGE,"E25.5"),sQuery(id+"F0.wireOp",EDGE,"E25.6"),sQuery(id+"F0.wireOp",EDGE,"E25.7")])],"isStart":false});
            extrude(context, id + "F17", {"entities" : qUnion([Q0, Q1, Q2]), "endBound" : BoundingType.UP_TO_SURFACE, "endBoundEntityFace" : qUnion([Q3]), "depth" : 25 * mm, "offsetDistance" : 25 * mm});
        }
    });
